# Revit family: NLRSen_AT_UN_RTLD_Supply_Solid_Air
name_source: partatom
category: Air Terminals
revit_build: Autodesk Revit 2017 (Build: 20190508_0315(x64)
units: mm (PartAtom-declared; Revit-internal decimal feet)

## family parameters
Always vertical = Yes
Cut with Voids When Loaded = No
OmniClass Number = 23.75.70.21.27.11
OmniClass Title = Diffusers, Registers, and Grilles
Part Type = Normal
Room Calculation Point = Yes
Round Connector Dimension = Use Diameter
Shared = No
Work Plane-Based = No

## types (6) — shared parameters
Assembly Code = 57.71
Description = Round flanged Louvre supply grill, Type RTLD
IfcDescription = Round flanged Louvre supply grill, Type RTLD
IfcExportAs = IfcAirterminal
IfcExportType = Diffuser
Lookup_Article_Codes = Grill_Article_Codes
Lookup_Article_Data = RTLD_Article_Data
Lookup_Article_Names = Grill_Article_Names
Lookup_Grill_Factors = Grill_Selection_Factors
Manufacturer = Solid Air Climate Solutions
Model = RTLD
NLRS_C_content_datum_uitgifte = 2019-10-01
NLRS_C_content_provider = Solid Air Climate Solutions
NLRS_C_content_versie = 2.03
NLRS_C_description = Round flanged Louvre supply grill, Type RTLD
SACS_AX_Prefix = 805
SACS_DbA_Text = Db(A)
SACS_Plenum_Material = Sendzimir verzinkt
SACS_Revised_ by = J. Feeke
SACS_Revision_Date = 2019-10-01
SACS_Revision_Number = 2.03
Type Comments = Please make sure flow is set to m3/h!
URL = https://solid-air.nl
zero-valued in all types: Cost

## per-type parameters (varying)
| type | Max Flow | Min Flow | SACS_Base_Index | SACS_Plenum_A | SACS_Plenum_D1 | SACS_Plenum_D2 | SACS_Plenum_G | SACS_Plenum_H | SACS_Plenum_K |
| 160 | 360 m³/h | 108 m³/h | 1 | 220 mm  [stored 0.721785 ft] | 158 mm | 158 mm | 206 mm  [stored 0.675853 ft] | 206 mm  [stored 0.675853 ft] | 101 mm  [stored 0.331365 ft] |
| 200 | 540 m³/h | 180 m³/h | 2 | 260 mm  [stored 0.853018 ft] | 198 mm  [stored 0.649606 ft] | 198 mm  [stored 0.649606 ft] | 245 mm  [stored 0.803806 ft] | 245 mm  [stored 0.803806 ft] | 115 mm  [stored 0.377297 ft] |
| 250 | 900 m³/h | 288 m³/h | 3 | 310 mm  [stored 1.01706 ft] | 248 mm  [stored 0.813648 ft] | 248 mm  [stored 0.813648 ft] | 296 mm  [stored 0.971129 ft] | 296 mm  [stored 0.971129 ft] | 114 mm  [stored 0.374016 ft] |
| 315 | 1440 m³/h | 450 m³/h | 4 | 375 mm  [stored 1.23031 ft] | 313 mm  [stored 1.0269 ft] | 313 mm  [stored 1.0269 ft] | 361 mm  [stored 1.18438 ft] | 361 mm  [stored 1.18438 ft] | 137 mm  [stored 0.449475 ft] |
| 400 | 1800 m³/h | 720 m³/h | 5 | 460 mm  [stored 1.50919 ft] | 398 mm  [stored 1.30577 ft] | 398 mm  [stored 1.30577 ft] | 446 mm  [stored 1.46325 ft] | 446 mm  [stored 1.46325 ft] | 131 mm  [stored 0.42979 ft] |
| 500 | 2520 m³/h | 1080 m³/h | 6 | 560 mm  [stored 1.83727 ft] | 498 mm  [stored 1.63386 ft] | 498 mm  [stored 1.63386 ft] | 546 mm  [stored 1.79134 ft] | 546 mm  [stored 1.79134 ft] | 163 mm  [stored 0.534777 ft] |

note: [stored X ft] marks values corroborated as IEEE doubles in the binary element streams (Revit-internal decimal feet)

## geometry (parser evidence)
native form markers: Sweep x15
no freeform markers — native parametric forms only
